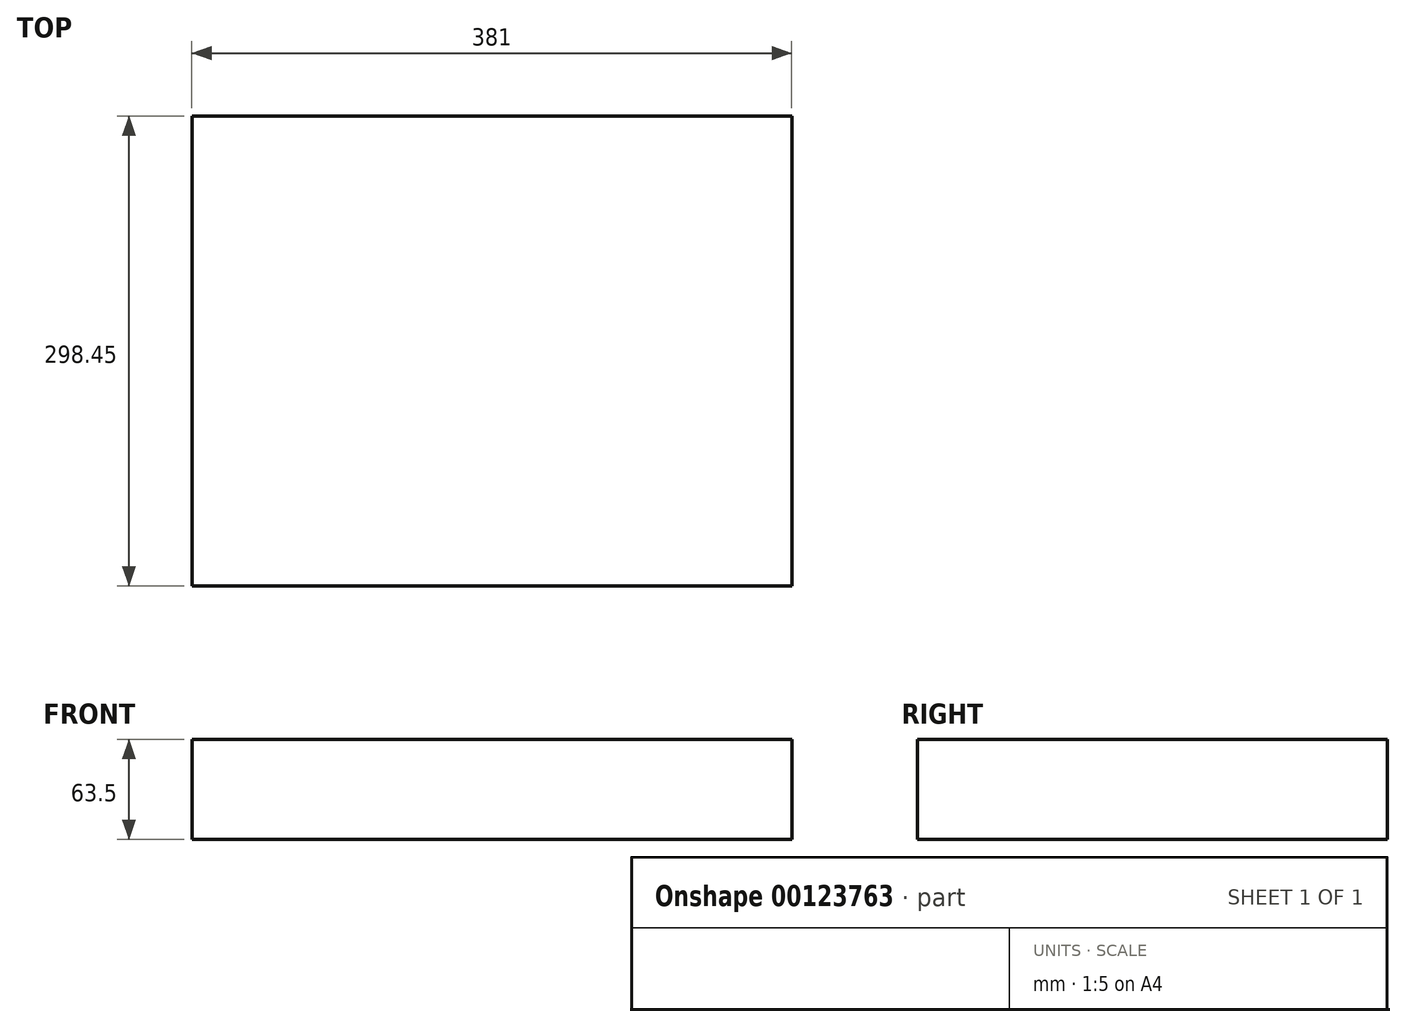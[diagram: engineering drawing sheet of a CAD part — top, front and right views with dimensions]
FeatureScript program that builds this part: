
annotation { "Feature Type Name" : "Feature", "Feature Type Description" : "" }
export const myFeature = defineFeature(function(context is Context, id is Id, definition is map)
    precondition{}
    {
        {
            var Q0;
            Q0=qCreatedBy(makeId("Top.planeOp"),FACE);
            var sketch = newSketch(context, id + "F0", { "sketchPlane" : qUnion([Q0])});
            skLineSegment(sketch, "E0.bottom", {"start": v(-195.3, 74.5) * mm, "end": v(185.7, 74.5) * mm});
            skLineSegment(sketch, "E0.top", {"start": v(-195.3, -223.95) * mm, "end": v(185.7, -223.95) * mm});
            skLineSegment(sketch, "E0.left", {"start": v(-195.3, 74.5) * mm, "end": v(-195.3, -223.95) * mm});
            skLineSegment(sketch, "E0.right", {"start": v(185.7, 74.5) * mm, "end": v(185.7, -223.95) * mm});
            skSolve(sketch);
        }
        {
            var Q0;
            Q0=makeQuery(id+"F0.imprint","IMPRINT",FACE,{"disambiguationData":[TD([[makeQuery(id+"F0.imprint","IMPRINT",EDGE,{"derivedFrom":sQuery(id+"F0.wireOp",EDGE,"E0.bottom")}),-1.0]])]});
            extrude(context, id + "F1", {"entities" : qUnion([Q0]), "depth" : 63.5 * mm});
        }
    });
